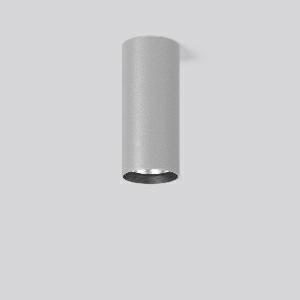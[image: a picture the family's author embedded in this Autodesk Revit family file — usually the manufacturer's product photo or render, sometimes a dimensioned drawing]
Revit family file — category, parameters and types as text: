
# Revit family: heledon_mini_a_931208_004_1_76_20ac
name_source: partatom
category: Lighting Fixtures
units: mm (PartAtom-declared; Revit-internal decimal feet)

## family parameters
Cut with Voids When Loaded = No
Host = Face
Light Source = No
Part Type = Normal
Room Calculation Point = No
Round Connector Dimension = Use Diameter
Shared = No

## types (1)
- HELEDON mini A (1 x LED Modul 940, 3800 lm, 4000)
    Apparent Load = 29 VA
    Approval mark = CE
    CIE Flux Codes = 100 100 100 100 100
    Color Rendering = 92
    Color Temperature = 4000
    Default Elevation = 1800 mm
    Description = Series: HELEDON mini
Cylindrical surface-mounted downlight. Housing: die-cast aluminium, powder-coated. Internal ceiling frame polycarbonate with bayonet mounting. Black plastic ring and recessed LED to prevent glare from the side. Optical assembly with reflector made of MIRO-Silver with 98% total light reflection for outstanding efficiency - can be changed without tools. Best colour rendering index Ra>90. Suitable for Ceiling mounting. Easy installation with a separate ceiling frame with bayonet mounting and plug connection. Driver integrated. Connected via plug-in connector. High quality converter without flickering and stroboscopic effect. The following accessories can be mounted without use of tools: interchangeable lenses, decorative glasses, honeycomb louvre, clear and frosted diffusers, white interchangeable plastic ring. 
Colour: silver
Diameter: 87 mm
Height: 197 mm
Lamp: LED
Socket: without socket
Colour temperature: 4000K
Colour rendering index (CRI): 92
System power: 29 W
Rated luminous flux: 3800 lm
Luminous efficiency: 131 lm/W
Control gear: Converter, dimmable, DALI
Protection class: I
Type of protection: IP 20
    Height = 197 mm
    Lamp = 1 x LED Modul 940
    Lamp Light Flux = 3800 lm
    Lamp count = 1
    Length = 87 mm
    Lifetime = 50000 h
    Luminous efficacy = 131 lm/W
    Manufacturer = RZB
    ModVariant = No
    Model = 931208.004.1.76
    Mounting Place = Ceiling
    Mounting Type = Surface mounted
    Number of Poles = 1
    OnlyDefault = Yes
    Power Factor = 1
    Product Name = HELEDON mini A
    Product group = Surface mounted downlights
    ProductGroupID = 302
    Protection Class = Protection class I
    Protection Degree = IP 20
    RLX_Detail_Level = 1
    RLX_Emergency_Light_Flux = 0 lm
    RLX_Emergency_Type = 0
    RLX_Emergency_Type_DB = No
    RlxData = <blob elided: 107753 chars, md5=2c0aba47>
    Socket = socket
    Standby Power = 0 W
    System Light Flux = 3800 lm
    System Power = 29 W
    Type Comments = Product without accessories
    Type Image = 931188.004.jpg
    URL = http://relux.com
    VarID = ---
    Voltage = 230 V
    Voltage Range = 220-240 V
    Weight = 0.00 kg
    Width = 0 mm  [stored 0 ft]

note: [stored X ft] marks values corroborated as IEEE doubles in the binary element streams (Revit-internal decimal feet)

## geometry (parser evidence)
native form markers: Blend x4, Sweep x9
no freeform markers — native parametric forms only
